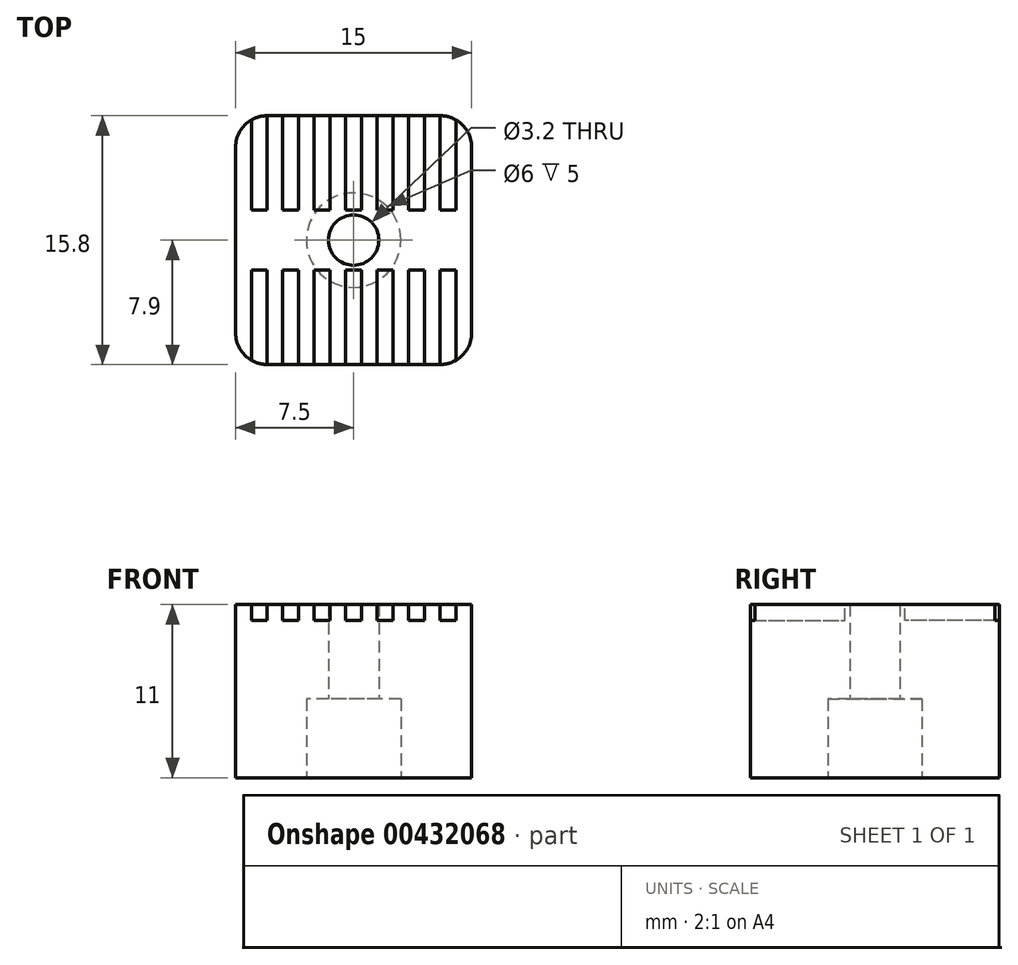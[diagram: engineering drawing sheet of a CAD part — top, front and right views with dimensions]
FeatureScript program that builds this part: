
annotation { "Feature Type Name" : "Feature", "Feature Type Description" : "" }
export const myFeature = defineFeature(function(context is Context, id is Id, definition is map)
    precondition{}
    {
        {
            var Q0;
            Q0=qCreatedBy(makeId("Top.planeOp"),FACE);
            var sketch = newSketch(context, id + "F0", { "sketchPlane" : qUnion([Q0])});
            skLineSegment(sketch, "E0.bottom", {"start": v(7.5, -7.9) * mm, "end": v(-7.5, -7.9) * mm});
            skLineSegment(sketch, "E0.top", {"start": v(7.5, 7.9) * mm, "end": v(-7.5, 7.9) * mm});
            skLineSegment(sketch, "E0.left", {"start": v(7.5, -7.9) * mm, "end": v(7.5, 7.9) * mm});
            skLineSegment(sketch, "E0.right", {"start": v(-7.5, -7.9) * mm, "end": v(-7.5, 7.9) * mm});
            skPoint(sketch, "E0.middle", {"position": v(0, 0) * mm});
            skCircle(sketch, "E1", {"center": v(0, 0) * mm, "radius": 1.6 * mm});
            skCircle(sketch, "E2", {"center": v(0, 0) * mm, "radius": 3 * mm});
            skSolve(sketch);
        }
        {
            var Q0;
            Q0=makeQuery(id+"F0.imprint","IMPRINT",FACE,{"disambiguationData":[TD([[makeQuery(id+"F0.imprint","IMPRINT",EDGE,{"derivedFrom":sQuery(id+"F0.wireOp",EDGE,"E0.bottom")}),-1.0]])]});
            var Q1;
            Q1=makeQuery(id+"F0.imprint","IMPRINT",FACE,{"disambiguationData":[TD([[makeQuery(id+"F0.imprint","IMPRINT",EDGE,{"derivedFrom":sQuery(id+"F0.wireOp",EDGE,"E1")}),-1.0]])]});
            extrude(context, id + "F1", {"entities" : qUnion([Q0, Q1]), "depth" : 11 * mm});
        }
        {
            var Q0;
            Q0=makeQuery(id+"F0.imprint","IMPRINT",FACE,{"disambiguationData":[TD([[makeQuery(id+"F0.imprint","IMPRINT",EDGE,{"derivedFrom":sQuery(id+"F0.wireOp",EDGE,"E1")}),-1.0]])]});
            extrude(context, id + "F2", {"entities" : qUnion([Q0]), "operationType" : NewBodyOperationType.REMOVE, "depth" : 5 * mm});
        }
        {
            var Q0;
            Q0=makeQuery(id+"F1.opExtrude","SWEPT_EDGE",EDGE,{"disambiguationData":[OSD([sQuery(id+"F0.wireOp",EDGE,"E0.top"),sQuery(id+"F0.wireOp",EDGE,"E0.right")])]});
            var Q1;
            Q1=makeQuery(id+"F1.opExtrude","SWEPT_EDGE",EDGE,{"disambiguationData":[OSD([sQuery(id+"F0.wireOp",EDGE,"E0.bottom"),sQuery(id+"F0.wireOp",EDGE,"E0.right")])]});
            var Q2;
            Q2=makeQuery(id+"F1.opExtrude","SWEPT_EDGE",EDGE,{"disambiguationData":[OSD([sQuery(id+"F0.wireOp",EDGE,"E0.bottom"),sQuery(id+"F0.wireOp",EDGE,"E0.left")])]});
            var Q3;
            Q3=makeQuery(id+"F1.opExtrude","SWEPT_EDGE",EDGE,{"disambiguationData":[OSD([sQuery(id+"F0.wireOp",EDGE,"E0.top"),sQuery(id+"F0.wireOp",EDGE,"E0.left")])]});
            fillet(context, id + "F3", {"entities" : qUnion([Q0, Q1, Q2, Q3]), "radius" : 2 * mm, "tangentPropagation" : true, "allowEdgeOverflow" : false});
        }
        {
            var Q0;
            Q0=makeQuery(id+"F1.opExtrude","CAP_FACE",FACE,{"disambiguationData":[OSD([sQuery(id+"F0.wireOp",EDGE,"E0.bottom"),sQuery(id+"F0.wireOp",EDGE,"E0.top"),sQuery(id+"F0.wireOp",EDGE,"E0.left"),sQuery(id+"F0.wireOp",EDGE,"E0.right"),sQuery(id+"F0.wireOp",EDGE,"E1")])],"isStart":false});
            var sketch = newSketch(context, id + "F4", { "sketchPlane" : qUnion([Q0])});
            skLineSegment(sketch, "E3.bottom", {"start": v(0, 7.9) * mm, "end": v(0.5, 7.9) * mm});
            skLineSegment(sketch, "E3.top", {"start": v(0, 1.9) * mm, "end": v(0.5, 1.9) * mm});
            skLineSegment(sketch, "E3.left", {"start": v(0, 7.9) * mm, "end": v(0, 1.9) * mm});
            skLineSegment(sketch, "E3.right", {"start": v(0.5, 7.9) * mm, "end": v(0.5, 1.9) * mm});
            skLineSegment(sketch, "E4.MirrorCS", {"start": v(-0.5, 7.9) * mm, "end": v(-0.5, 1.9) * mm});
            skLineSegment(sketch, "E5.MirrorCS", {"start": v(0, 1.9) * mm, "end": v(-0.5, 1.9) * mm});
            skLineSegment(sketch, "E6.MirrorCS", {"start": v(0, 7.9) * mm, "end": v(-0.5, 7.9) * mm});
            skLineSegment(sketch, "E7.MirrorCS", {"start": v(0, -7.9) * mm, "end": v(-0.5, -7.9) * mm});
            skLineSegment(sketch, "E8.MirrorCS", {"start": v(0, -7.9) * mm, "end": v(0.5, -7.9) * mm});
            skLineSegment(sketch, "E9.MirrorCS", {"start": v(0.5, -7.9) * mm, "end": v(0.5, -1.9) * mm});
            skLineSegment(sketch, "E10.MirrorCS", {"start": v(0, -1.9) * mm, "end": v(0.5, -1.9) * mm});
            skLineSegment(sketch, "E11.MirrorCS", {"start": v(0, -1.9) * mm, "end": v(-0.5, -1.9) * mm});
            skLineSegment(sketch, "E12.MirrorCS", {"start": v(-0.5, -7.9) * mm, "end": v(-0.5, -1.9) * mm});
            skLineSegment(sketch, "E13.1.0.0", {"start": v(1.5, 7.9) * mm, "end": v(1.5, 1.9) * mm});
            skLineSegment(sketch, "E13.1.0.1", {"start": v(2, 7.9) * mm, "end": v(1.5, 7.9) * mm});
            skLineSegment(sketch, "E13.1.0.2", {"start": v(2, 7.9) * mm, "end": v(2.5, 7.9) * mm});
            skLineSegment(sketch, "E13.1.0.3", {"start": v(2, 1.9) * mm, "end": v(2.5, 1.9) * mm});
            skLineSegment(sketch, "E13.1.0.4", {"start": v(2, 1.9) * mm, "end": v(1.5, 1.9) * mm});
            skLineSegment(sketch, "E13.1.0.5", {"start": v(2.5, 7.9) * mm, "end": v(2.5, 1.9) * mm});
            skLineSegment(sketch, "E13.1.0.6", {"start": v(1.5, -7.9) * mm, "end": v(1.5, -1.9) * mm});
            skLineSegment(sketch, "E13.1.0.7", {"start": v(2, -1.9) * mm, "end": v(1.5, -1.9) * mm});
            skLineSegment(sketch, "E13.1.0.8", {"start": v(2, -1.9) * mm, "end": v(2.5, -1.9) * mm});
            skLineSegment(sketch, "E13.1.0.9", {"start": v(2.5, -7.9) * mm, "end": v(2.5, -1.9) * mm});
            skLineSegment(sketch, "E13.1.0.10", {"start": v(2, -7.9) * mm, "end": v(1.5, -7.9) * mm});
            skLineSegment(sketch, "E13.1.0.11", {"start": v(2, -7.9) * mm, "end": v(2.5, -7.9) * mm});
            skLineSegment(sketch, "E13.2.0.0", {"start": v(3.5, 7.9) * mm, "end": v(3.5, 1.9) * mm});
            skLineSegment(sketch, "E13.2.0.1", {"start": v(4, 7.9) * mm, "end": v(3.5, 7.9) * mm});
            skLineSegment(sketch, "E13.2.0.2", {"start": v(4, 7.9) * mm, "end": v(4.5, 7.9) * mm});
            skLineSegment(sketch, "E13.2.0.3", {"start": v(4, 1.9) * mm, "end": v(4.5, 1.9) * mm});
            skLineSegment(sketch, "E13.2.0.4", {"start": v(4, 1.9) * mm, "end": v(3.5, 1.9) * mm});
            skLineSegment(sketch, "E13.2.0.5", {"start": v(4.5, 7.9) * mm, "end": v(4.5, 1.9) * mm});
            skLineSegment(sketch, "E13.2.0.6", {"start": v(3.5, -7.9) * mm, "end": v(3.5, -1.9) * mm});
            skLineSegment(sketch, "E13.2.0.7", {"start": v(4, -1.9) * mm, "end": v(3.5, -1.9) * mm});
            skLineSegment(sketch, "E13.2.0.8", {"start": v(4, -1.9) * mm, "end": v(4.5, -1.9) * mm});
            skLineSegment(sketch, "E13.2.0.9", {"start": v(4.5, -7.9) * mm, "end": v(4.5, -1.9) * mm});
            skLineSegment(sketch, "E13.2.0.10", {"start": v(4, -7.9) * mm, "end": v(3.5, -7.9) * mm});
            skLineSegment(sketch, "E13.2.0.11", {"start": v(4, -7.9) * mm, "end": v(4.5, -7.9) * mm});
            skLineSegment(sketch, "E13.3.0.0", {"start": v(5.5, 7.9) * mm, "end": v(5.5, 1.9) * mm});
            skLineSegment(sketch, "E13.3.0.1", {"start": v(6, 7.9) * mm, "end": v(5.5, 7.9) * mm});
            skLineSegment(sketch, "E13.3.0.2", {"start": v(6, 7.9) * mm, "end": v(6.5, 7.9) * mm});
            skLineSegment(sketch, "E13.3.0.3", {"start": v(6, 1.9) * mm, "end": v(6.5, 1.9) * mm});
            skLineSegment(sketch, "E13.3.0.4", {"start": v(6, 1.9) * mm, "end": v(5.5, 1.9) * mm});
            skLineSegment(sketch, "E13.3.0.5", {"start": v(6.5, 7.9) * mm, "end": v(6.5, 1.9) * mm});
            skLineSegment(sketch, "E13.3.0.6", {"start": v(5.5, -7.9) * mm, "end": v(5.5, -1.9) * mm});
            skLineSegment(sketch, "E13.3.0.7", {"start": v(6, -1.9) * mm, "end": v(5.5, -1.9) * mm});
            skLineSegment(sketch, "E13.3.0.8", {"start": v(6, -1.9) * mm, "end": v(6.5, -1.9) * mm});
            skLineSegment(sketch, "E13.3.0.9", {"start": v(6.5, -7.9) * mm, "end": v(6.5, -1.9) * mm});
            skLineSegment(sketch, "E13.3.0.10", {"start": v(6, -7.9) * mm, "end": v(5.5, -7.9) * mm});
            skLineSegment(sketch, "E13.3.0.11", {"start": v(6, -7.9) * mm, "end": v(6.5, -7.9) * mm});
            skLineSegment(sketch, "E14.1.0.0", {"start": v(-2.5, 7.9) * mm, "end": v(-2.5, 1.9) * mm});
            skLineSegment(sketch, "E14.1.0.1", {"start": v(-2, 7.9) * mm, "end": v(-2.5, 7.9) * mm});
            skLineSegment(sketch, "E14.1.0.2", {"start": v(-2, 7.9) * mm, "end": v(-1.5, 7.9) * mm});
            skLineSegment(sketch, "E14.1.0.3", {"start": v(-1.5, 7.9) * mm, "end": v(-1.5, 1.9) * mm});
            skLineSegment(sketch, "E14.1.0.4", {"start": v(-2.5, -7.9) * mm, "end": v(-2.5, -1.9) * mm});
            skLineSegment(sketch, "E14.1.0.5", {"start": v(-1.5, -7.9) * mm, "end": v(-1.5, -1.9) * mm});
            skLineSegment(sketch, "E14.1.0.6", {"start": v(-2, -1.9) * mm, "end": v(-1.5, -1.9) * mm});
            skLineSegment(sketch, "E14.1.0.7", {"start": v(-2, -1.9) * mm, "end": v(-2.5, -1.9) * mm});
            skLineSegment(sketch, "E14.1.0.8", {"start": v(-2, -7.9) * mm, "end": v(-2.5, -7.9) * mm});
            skLineSegment(sketch, "E14.1.0.9", {"start": v(-2, -7.9) * mm, "end": v(-1.5, -7.9) * mm});
            skLineSegment(sketch, "E14.2.0.0", {"start": v(-4.5, 7.9) * mm, "end": v(-4.5, 1.9) * mm});
            skLineSegment(sketch, "E14.2.0.1", {"start": v(-4, 7.9) * mm, "end": v(-4.5, 7.9) * mm});
            skLineSegment(sketch, "E14.2.0.2", {"start": v(-4, 7.9) * mm, "end": v(-3.5, 7.9) * mm});
            skLineSegment(sketch, "E14.2.0.3", {"start": v(-3.5, 7.9) * mm, "end": v(-3.5, 1.9) * mm});
            skLineSegment(sketch, "E14.2.0.4", {"start": v(-4.5, -7.9) * mm, "end": v(-4.5, -1.9) * mm});
            skLineSegment(sketch, "E14.2.0.5", {"start": v(-3.5, -7.9) * mm, "end": v(-3.5, -1.9) * mm});
            skLineSegment(sketch, "E14.2.0.6", {"start": v(-4, -1.9) * mm, "end": v(-3.5, -1.9) * mm});
            skLineSegment(sketch, "E14.2.0.7", {"start": v(-4, -1.9) * mm, "end": v(-4.5, -1.9) * mm});
            skLineSegment(sketch, "E14.2.0.8", {"start": v(-4, -7.9) * mm, "end": v(-4.5, -7.9) * mm});
            skLineSegment(sketch, "E14.2.0.9", {"start": v(-4, -7.9) * mm, "end": v(-3.5, -7.9) * mm});
            skLineSegment(sketch, "E14.3.0.0", {"start": v(-6.5, 7.9) * mm, "end": v(-6.5, 1.9) * mm});
            skLineSegment(sketch, "E14.3.0.1", {"start": v(-6, 7.9) * mm, "end": v(-6.5, 7.9) * mm});
            skLineSegment(sketch, "E14.3.0.2", {"start": v(-6, 7.9) * mm, "end": v(-5.5, 7.9) * mm});
            skLineSegment(sketch, "E14.3.0.3", {"start": v(-5.5, 7.9) * mm, "end": v(-5.5, 1.9) * mm});
            skLineSegment(sketch, "E14.3.0.4", {"start": v(-6.5, -7.9) * mm, "end": v(-6.5, -1.9) * mm});
            skLineSegment(sketch, "E14.3.0.5", {"start": v(-5.5, -7.9) * mm, "end": v(-5.5, -1.9) * mm});
            skLineSegment(sketch, "E14.3.0.6", {"start": v(-6, -1.9) * mm, "end": v(-5.5, -1.9) * mm});
            skLineSegment(sketch, "E14.3.0.7", {"start": v(-6, -1.9) * mm, "end": v(-6.5, -1.9) * mm});
            skLineSegment(sketch, "E14.3.0.8", {"start": v(-6, -7.9) * mm, "end": v(-6.5, -7.9) * mm});
            skLineSegment(sketch, "E14.3.0.9", {"start": v(-6, -7.9) * mm, "end": v(-5.5, -7.9) * mm});
            skLineSegment(sketch, "E15.1.0.0", {"start": v(-2, 1.9) * mm, "end": v(-2.5, 1.9) * mm});
            skLineSegment(sketch, "E15.1.0.1", {"start": v(-2, 1.9) * mm, "end": v(-1.5, 1.9) * mm});
            skLineSegment(sketch, "E15.2.0.0", {"start": v(-4, 1.9) * mm, "end": v(-4.5, 1.9) * mm});
            skLineSegment(sketch, "E15.2.0.1", {"start": v(-4, 1.9) * mm, "end": v(-3.5, 1.9) * mm});
            skLineSegment(sketch, "E15.3.0.0", {"start": v(-6, 1.9) * mm, "end": v(-6.5, 1.9) * mm});
            skLineSegment(sketch, "E15.3.0.1", {"start": v(-6, 1.9) * mm, "end": v(-5.5, 1.9) * mm});
            skLineSegment(sketch, "E15.direction1", {"start": v(-0.5, 1.9) * mm, "end": v(-2.5, 1.9) * mm, "construction": true});
            skSolve(sketch);
        }
        {
            var Q0;
            Q0=makeQuery(id+"F4.imprint","IMPRINT",FACE,{"disambiguationData":[TD([[makeQuery(id+"F4.imprint","IMPRINT",EDGE,{"derivedFrom":sQuery(id+"F4.wireOp",EDGE,"E3.left")}),-1.0]])]});
            var Q1;
            Q1=makeQuery(id+"F4.imprint","IMPRINT",FACE,{"disambiguationData":[TD([[makeQuery(id+"F4.imprint","IMPRINT",EDGE,{"derivedFrom":sQuery(id+"F4.wireOp",EDGE,"E3.bottom")}),1.0]])]});
            var Q2;
            Q2=makeQuery(id+"F4.imprint","IMPRINT",FACE,{"disambiguationData":[TD([[makeQuery(id+"F4.imprint","IMPRINT",EDGE,{"derivedFrom":sQuery(id+"F4.wireOp",EDGE,"E13.1.0.0")}),1.0]])]});
            var Q3;
            Q3=makeQuery(id+"F4.imprint","IMPRINT",FACE,{"disambiguationData":[TD([[makeQuery(id+"F4.imprint","IMPRINT",EDGE,{"derivedFrom":sQuery(id+"F4.wireOp",EDGE,"E13.2.0.0")}),1.0]])]});
            var Q4;
            {var subQ6=sQuery(id+"F4.wireOp",EDGE,"E13.3.0.0");Q4=makeQuery(id+"F4.imprint","IMPRINT",FACE,{"disambiguationData":[TD([[makeQuery(id+"F4.imprint","IMPRINT",EDGE,{"derivedFrom":subQ6}),1.0]])]});}
            var Q5;
            Q5=makeQuery(id+"F4.imprint","IMPRINT",FACE,{"disambiguationData":[TD([[makeQuery(id+"F4.imprint","IMPRINT",EDGE,{"derivedFrom":sQuery(id+"F4.wireOp",EDGE,"E14.1.0.0")}),1.0]])]});
            var Q6;
            Q6=makeQuery(id+"F4.imprint","IMPRINT",FACE,{"disambiguationData":[TD([[makeQuery(id+"F4.imprint","IMPRINT",EDGE,{"derivedFrom":sQuery(id+"F4.wireOp",EDGE,"E14.2.0.0")}),1.0]])]});
            var Q7;
            {var subQ1=sQuery(id+"F4.wireOp",EDGE,"E14.3.0.3");Q7=makeQuery(id+"F4.imprint","IMPRINT",FACE,{"disambiguationData":[TD([[makeQuery(id+"F4.imprint","IMPRINT",EDGE,{"derivedFrom":subQ1}),-1.0]])]});}
            var Q8;
            {var subQ1=sQuery(id+"F4.wireOp",EDGE,"E14.3.0.5");Q8=makeQuery(id+"F4.imprint","IMPRINT",FACE,{"disambiguationData":[TD([[makeQuery(id+"F4.imprint","IMPRINT",EDGE,{"derivedFrom":subQ1}),1.0]])]});}
            var Q9;
            Q9=makeQuery(id+"F4.imprint","IMPRINT",FACE,{"disambiguationData":[TD([[makeQuery(id+"F4.imprint","IMPRINT",EDGE,{"derivedFrom":sQuery(id+"F4.wireOp",EDGE,"E14.2.0.4")}),-1.0]])]});
            var Q10;
            Q10=makeQuery(id+"F4.imprint","IMPRINT",FACE,{"disambiguationData":[TD([[makeQuery(id+"F4.imprint","IMPRINT",EDGE,{"derivedFrom":sQuery(id+"F4.wireOp",EDGE,"E14.1.0.4")}),-1.0]])]});
            var Q11;
            Q11=makeQuery(id+"F4.imprint","IMPRINT",FACE,{"disambiguationData":[TD([[makeQuery(id+"F4.imprint","IMPRINT",EDGE,{"derivedFrom":sQuery(id+"F4.wireOp",EDGE,"E7.MirrorCS")}),-1.0]])]});
            var Q12;
            Q12=makeQuery(id+"F4.imprint","IMPRINT",FACE,{"disambiguationData":[TD([[makeQuery(id+"F4.imprint","IMPRINT",EDGE,{"derivedFrom":sQuery(id+"F4.wireOp",EDGE,"E13.1.0.6")}),-1.0]])]});
            var Q13;
            Q13=makeQuery(id+"F4.imprint","IMPRINT",FACE,{"disambiguationData":[TD([[makeQuery(id+"F4.imprint","IMPRINT",EDGE,{"derivedFrom":sQuery(id+"F4.wireOp",EDGE,"E13.2.0.6")}),-1.0]])]});
            var Q14;
            {var subQ6=sQuery(id+"F4.wireOp",EDGE,"E13.3.0.6");Q14=makeQuery(id+"F4.imprint","IMPRINT",FACE,{"disambiguationData":[TD([[makeQuery(id+"F4.imprint","IMPRINT",EDGE,{"derivedFrom":subQ6}),-1.0]])]});}
            extrude(context, id + "F5", {"entities" : qUnion([Q0, Q1, Q2, Q3, Q4, Q5, Q6, Q7, Q8, Q9, Q10, Q11, Q12, Q13, Q14]), "operationType" : NewBodyOperationType.REMOVE, "oppositeDirection" : true, "depth" : 1 * mm});
        }
    });
